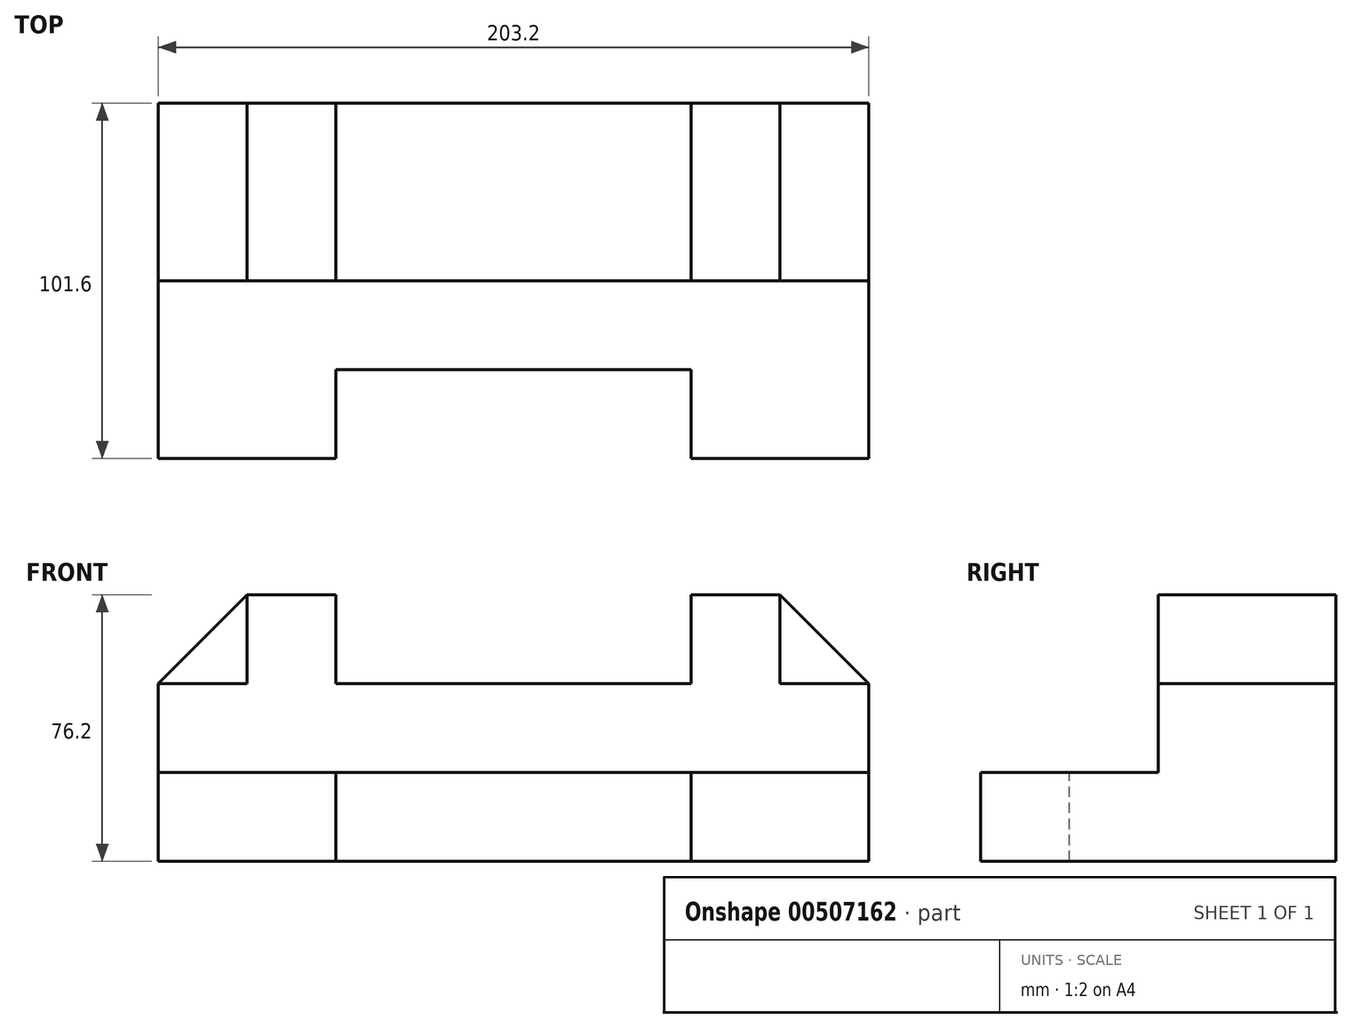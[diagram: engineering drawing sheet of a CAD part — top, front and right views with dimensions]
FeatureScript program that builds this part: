
annotation { "Feature Type Name" : "Feature", "Feature Type Description" : "" }
export const myFeature = defineFeature(function(context is Context, id is Id, definition is map)
    precondition{}
    {
        {
            var Q0;
            Q0=qCreatedBy(makeId("Top.planeOp"),FACE);
            var sketch = newSketch(context, id + "F0", { "sketchPlane" : qUnion([Q0])});
            skLineSegment(sketch, "E0", {"start": v(-68.34, 53.47) * mm, "end": v(-68.34, 2.67) * mm});
            skLineSegment(sketch, "E1", {"start": v(-68.34, 2.67) * mm, "end": v(134.86, 2.67) * mm});
            skLineSegment(sketch, "E2", {"start": v(134.86, 2.67) * mm, "end": v(134.86, 53.47) * mm});
            skLineSegment(sketch, "E3", {"start": v(134.86, 53.47) * mm, "end": v(-68.34, 53.47) * mm});
            skSolve(sketch);
        }
        {
            var Q0;
            Q0=makeQuery(id+"F0.imprint","IMPRINT",FACE,{"disambiguationData":[TD([[makeQuery(id+"F0.imprint","IMPRINT",EDGE,{"derivedFrom":sQuery(id+"F0.wireOp",EDGE,"E0")}),1.0]])]});
            extrude(context, id + "F1", {"entities" : qUnion([Q0]), "depth" : 50.8 * mm, "offsetDistance" : 25.4 * mm});
        }
        {
            var Q0;
            Q0=makeQuery(id+"F1.opExtrude","CAP_FACE",FACE,{"disambiguationData":[OSD([sQuery(id+"F0.wireOp",EDGE,"E0"),sQuery(id+"F0.wireOp",EDGE,"E1"),sQuery(id+"F0.wireOp",EDGE,"E2"),sQuery(id+"F0.wireOp",EDGE,"E3")])],"isStart":false});
            var sketch = newSketch(context, id + "F2", { "sketchPlane" : qUnion([Q0])});
            skLineSegment(sketch, "E4", {"start": v(109.46, 53.47) * mm, "end": v(109.46, 2.67) * mm});
            skLineSegment(sketch, "E5", {"start": v(109.46, 2.67) * mm, "end": v(84.06, 2.67) * mm});
            skLineSegment(sketch, "E6", {"start": v(84.06, 2.67) * mm, "end": v(84.06, 53.47) * mm});
            skLineSegment(sketch, "E7", {"start": v(84.06, 53.47) * mm, "end": v(109.46, 53.47) * mm});
            skSolve(sketch);
        }
        {
            var Q0;
            Q0=makeQuery(id+"F2.imprint","IMPRINT",FACE,{"disambiguationData":[TD([[makeQuery(id+"F2.imprint","IMPRINT",EDGE,{"derivedFrom":sQuery(id+"F2.wireOp",EDGE,"E4")}),-1.0]])]});
            extrude(context, id + "F3", {"entities" : qUnion([Q0]), "operationType" : NewBodyOperationType.ADD, "depth" : 25.4 * mm, "offsetDistance" : 25.4 * mm});
        }
        {
            var Q0;
            {var subQ0=sQuery(id+"F0.wireOp",EDGE,"E1");var subQ1=sQuery(id+"F0.wireOp",EDGE,"E3");var subQ2=sQuery(id+"F0.wireOp",EDGE,"E0");Q0=makeQuery(id+"F3.boolean.opBoolean","SPLIT",FACE,{"disambiguationData":[TD([makeQuery(id+"F1.opExtrude","SWEPT_FACE",FACE,{"disambiguationData":[OSD([subQ2])]})])],"derivedFrom":makeQuery(id+"F1.opExtrude","CAP_FACE",FACE,{"disambiguationData":[OSD([subQ2,subQ0,sQuery(id+"F0.wireOp",EDGE,"E2"),subQ1])],"isStart":false})});}
            var sketch = newSketch(context, id + "F4", { "sketchPlane" : qUnion([Q0])});
            skLineSegment(sketch, "E8", {"start": v(-42.94, 53.47) * mm, "end": v(-42.94, 2.67) * mm});
            skLineSegment(sketch, "E9", {"start": v(-42.94, 2.67) * mm, "end": v(-17.54, 2.67) * mm});
            skLineSegment(sketch, "E10", {"start": v(-17.54, 2.67) * mm, "end": v(-17.54, 53.47) * mm});
            skLineSegment(sketch, "E11", {"start": v(-17.54, 53.47) * mm, "end": v(-42.94, 53.47) * mm});
            skSolve(sketch);
        }
        {
            var Q0;
            Q0 = qSketchRegion(id + "F4", true);
            extrude(context, id + "F5", {"entities" : qUnion([Q0]), "operationType" : NewBodyOperationType.ADD, "depth" : 25.4 * mm, "offsetDistance" : 25.4 * mm});
        }
        {
            var Q0;
            Q0=makeQuery(id+"F5.boolean.opBoolean","MERGE",FACE,{"derivedFrom":[makeQuery(id+"F3.boolean.opBoolean","MERGE",FACE,{"derivedFrom":[makeQuery(id+"F1.opExtrude","SWEPT_FACE",FACE,{"disambiguationData":[OSD([sQuery(id+"F0.wireOp",EDGE,"E1")])]}),makeQuery(id+"F3.opExtrude","SWEPT_FACE",FACE,{"disambiguationData":[OSD([sQuery(id+"F2.wireOp",EDGE,"E5")])]})]}),makeQuery(id+"F5.opExtrude","SWEPT_FACE",FACE,{"disambiguationData":[OSD([sQuery(id+"F4.wireOp",EDGE,"E9")])]})]});
            var sketch = newSketch(context, id + "F6", { "sketchPlane" : qUnion([Q0])});
            skLineSegment(sketch, "E12", {"start": v(-68.34, 50.8) * mm, "end": v(-42.94, 76.2) * mm});
            skLineSegment(sketch, "E13", {"start": v(-42.94, 76.2) * mm, "end": v(-42.94, 50.8) * mm});
            skLineSegment(sketch, "E14", {"start": v(-42.94, 50.8) * mm, "end": v(-68.34, 50.8) * mm});
            skLineSegment(sketch, "E15", {"start": v(109.46, 76.2) * mm, "end": v(109.46, 50.8) * mm});
            skLineSegment(sketch, "E16", {"start": v(109.46, 50.8) * mm, "end": v(134.86, 50.8) * mm});
            skLineSegment(sketch, "E17", {"start": v(134.86, 50.8) * mm, "end": v(109.46, 76.2) * mm});
            skSolve(sketch);
        }
        {
            var Q0;
            Q0 = qSketchRegion(id + "F6", true);
            extrude(context, id + "F7", {"entities" : qUnion([Q0]), "oppositeDirection" : true, "depth" : 50.8 * mm, "offsetDistance" : 25.4 * mm});
        }
        {
            var Q0;
            Q0=makeQuery(id+"F1.opExtrude","SWEPT_FACE",FACE,{"disambiguationData":[OSD([sQuery(id+"F0.wireOp",EDGE,"E2")])]});
            var sketch = newSketch(context, id + "F8", { "sketchPlane" : qUnion([Q0])});
            skLineSegment(sketch, "E18", {"start": v(2.67, 0) * mm, "end": v(-48.13, 0) * mm});
            skLineSegment(sketch, "E19", {"start": v(-48.13, 0) * mm, "end": v(-48.13, 25.4) * mm});
            skLineSegment(sketch, "E20", {"start": v(-48.13, 25.4) * mm, "end": v(2.67, 25.4) * mm});
            skLineSegment(sketch, "E21", {"start": v(2.67, 25.4) * mm, "end": v(2.67, 0) * mm});
            skSolve(sketch);
        }
        {
            var Q0;
            Q0=makeQuery(id+"F8.imprint","IMPRINT",FACE,{"disambiguationData":[TD([[makeQuery(id+"F8.imprint","IMPRINT",EDGE,{"derivedFrom":sQuery(id+"F8.wireOp",EDGE,"E18")}),-1.0]])]});
            extrude(context, id + "F9", {"entities" : qUnion([Q0]), "operationType" : NewBodyOperationType.ADD, "oppositeDirection" : true, "depth" : 203.2 * mm, "offsetDistance" : 25.4 * mm});
        }
        {
            var Q0;
            Q0=makeQuery(id+"F9.opExtrude","SWEPT_FACE",FACE,{"disambiguationData":[OSD([sQuery(id+"F8.wireOp",EDGE,"E20")])]});
            var sketch = newSketch(context, id + "F10", { "sketchPlane" : qUnion([Q0])});
            skLineSegment(sketch, "E22", {"start": v(-17.54, -48.13) * mm, "end": v(-17.54, -22.73) * mm});
            skLineSegment(sketch, "E23", {"start": v(-17.54, -22.73) * mm, "end": v(84.06, -22.73) * mm});
            skLineSegment(sketch, "E24", {"start": v(84.06, -22.73) * mm, "end": v(84.06, -48.13) * mm});
            skLineSegment(sketch, "E25", {"start": v(84.06, -48.13) * mm, "end": v(-17.54, -48.13) * mm});
            skSolve(sketch);
        }
        {
            var Q0;
            Q0 = qSketchRegion(id + "F10", true);
            extrude(context, id + "F11", {"entities" : qUnion([Q0]), "operationType" : NewBodyOperationType.REMOVE, "oppositeDirection" : true, "depth" : 25.4 * mm, "offsetDistance" : 25.4 * mm});
        }
    });
